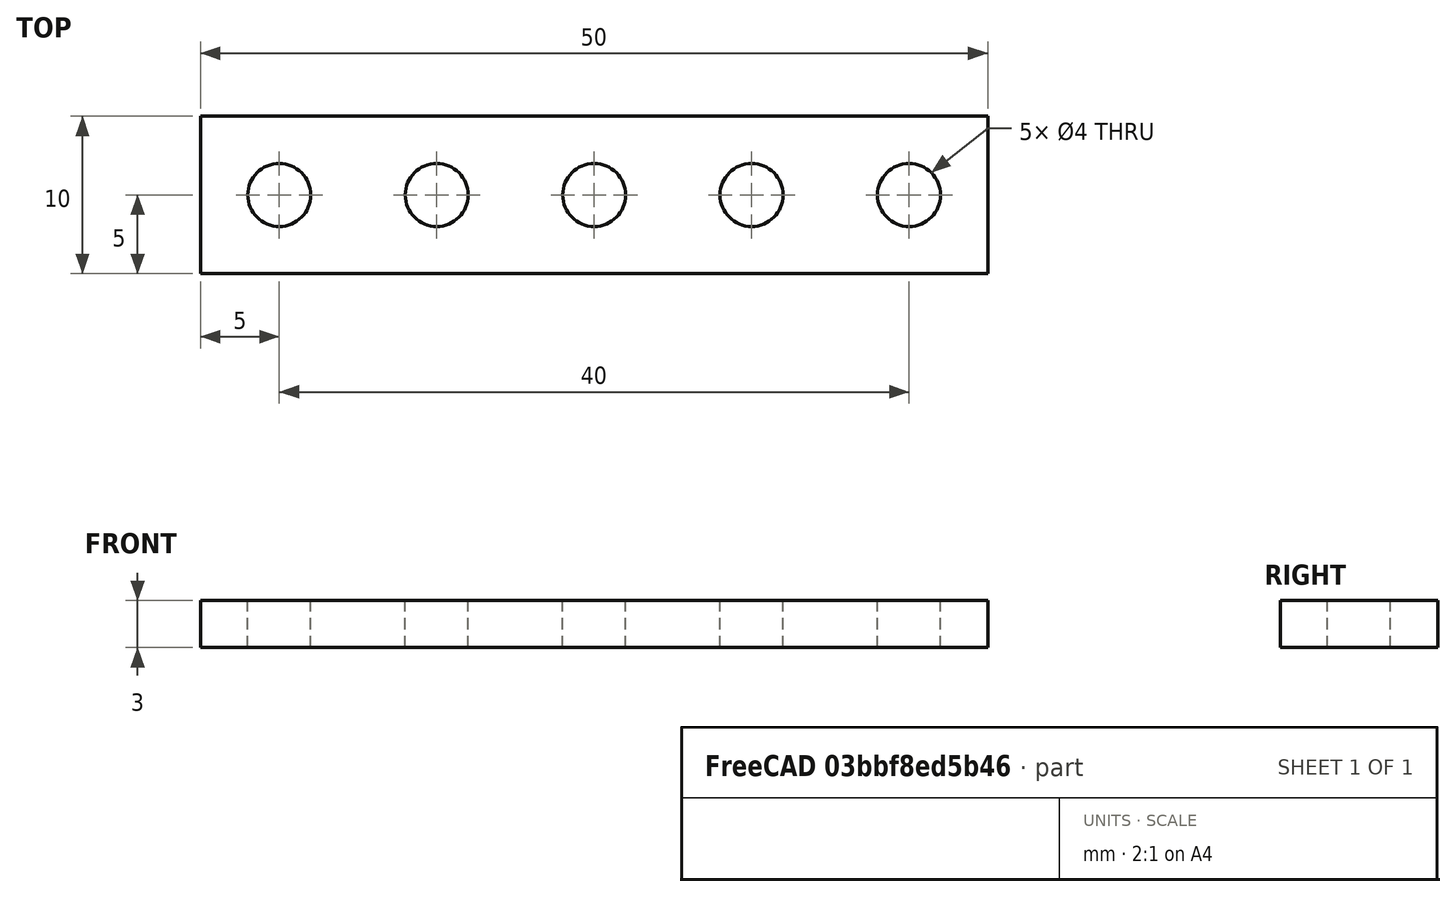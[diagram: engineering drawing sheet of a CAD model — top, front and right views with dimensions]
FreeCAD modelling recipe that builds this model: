
FCSTD DOCUMENT  (FreeCAD 0.16R6707 (Git))
Label: 06-Pieza-mecano
License: All rights reserved
LicenseURL: http://en.wikipedia.org/wiki/All_rights_reserved
objects: Part::Box×1, Part::Cylinder×1, Part::FeaturePython×1, Part::Cut×1
note: 4 computed .brp shape members not serialized (recipe doc carries the construction recipe); baked Part::Feature solids carry a one-line shape summary decoded from their .brp

FEATURE [Part::Box] Box  label="Base"
  Height = 3
  Length = 50
  Width = 10
FEATURE [Part::Cylinder] Cylinder  label="Cilindro"
  Angle = 360
  Height = 10
  Placement = pos=(5,5,0) rot=(0,0,1;0rad)
  Radius = 2
FEATURE [Part::FeaturePython] Array  # Draft array (typed FeaturePython)
  Angle = 360
  ArrayType = 0
  Axis = (0,0,1)
  Base = -> Cylinder
  Center = (0,0,0)
  Fuse = false
  IntervalAxis = (0,0,0)
  IntervalX = (10,0,0)
  IntervalY = (0,1,0)
  IntervalZ = (0,0,0)
  NumberPolar = 1
  NumberX = 5
  NumberY = 1
  NumberZ = 1
FEATURE [Part::Cut] Cut
  Base = -> Box
  Tool = -> Array
